# Revit family: PRD_AR_SpprtRls_MEDCAREGrabRail_MEDC0007_MEDC0008
name_source: partatom
category: Specialty Equipment
units: mm (PartAtom-declared; Revit-internal decimal feet)

## family parameters
Cut with Voids When Loaded = No
Enable Cutting in Views = No
Host = Face
Maintain Annotation Orientation = No
OmniClass Number = 23.40.20.21.47
OmniClass Title = Bath Grab Bars
Part Type = Normal
Room Calculation Point = No
Round Connector Dimension = Use Diameter
Shared = No

## types (2) — shared parameters
AssetType = Fixed
Back = no
BodyMaterial = PRD_AR_StainlessSteel_SatinFinished_BasaltGrey
Category = Pr_40_20_76_84, Support rails
Color = basalt grey
Default Elevation = 1200 mm
Description = MEDCARE 90° angled grab rail for wall mounting, stainless steel, basalt grey coated surface, 32 mm pipe diameter, 1.5 mm material thickness, 84 mm wall clearance, with plastic end caps, concealed mounting via stainless steel cylinders and rosettes, including mounting material.
Diameter = 32 mm  [stored 0.104987 ft]
Export Type to IFC As = IfcRailingType
Finish = satin finished
IfcExportAs = IfcRailingType
IfcExportType = HANDRAIL
IsExternal = FALSE
Manufacturer = KWC Group Management AG
ManufacturerName = KWC Group Management AG
ManufacturerURL = www.kwc-professional.com
Material = stainless steel
MaterialCode = 1.4301 Chrome Nickel steel V2A
NBSDescription = Support rails
NBSReference = 45-35-72/360
NominalDepth = 84 mm  [stored 0.275591 ft]
NominalHeight = 600 mm  [stored 1.9685 ft]
NominalWidth = 400 mm  [stored 1.31234 ft]
OverallDepth = 84 mm
OverallHeight = 623 mm
OverallWidth = 406 mm
PipeDiameter = 32 mm
ProductInformation = http://pim.kwc.com
Size = 400 x 600 x 84 mm (W x H x D)
Status = New
SurfaceFinish = satin finished
Type IFC Predefined Type = HANDRAIL
TypeOfFixing = screw
TypeOfGrabRail = angle bar
TypeOfMounting = wall mounting
URL = www.kwc-professional.com
Uniclass2015Code = Pr_40_20_76_84
Uniclass2015Title = Support rails
Uniclass2015Version = Products v1.36
Version = 1
zero-valued in all types: Height

## per-type parameters (varying)
| type | BIMObjectName | Direction | Features | ModelNumber | Name | left | right |
| MEDC0007 | PRD_AR_SupportRails_MEDCAREAngledGrabRail_MEDC0007 | right | Right-hand version. | 3600003775 | MEDCARE Angled grab rail MEDC0007 | No | Yes |
| MEDC0008 | PRD_AR_SupportRails_MEDCAREAngledGrabRail_MEDC0008 | left | Left-hand version. | 3600003776 | MEDCARE Angled grab rail MEDC0008 | Yes | No |

note: column(s) folded — value = type name in every type: Model, ModelReference

note: [stored X ft] marks values corroborated as IEEE doubles in the binary element streams (Revit-internal decimal feet)

## geometry (parser evidence)
native form markers: Sweep x6
no freeform markers — native parametric forms only
